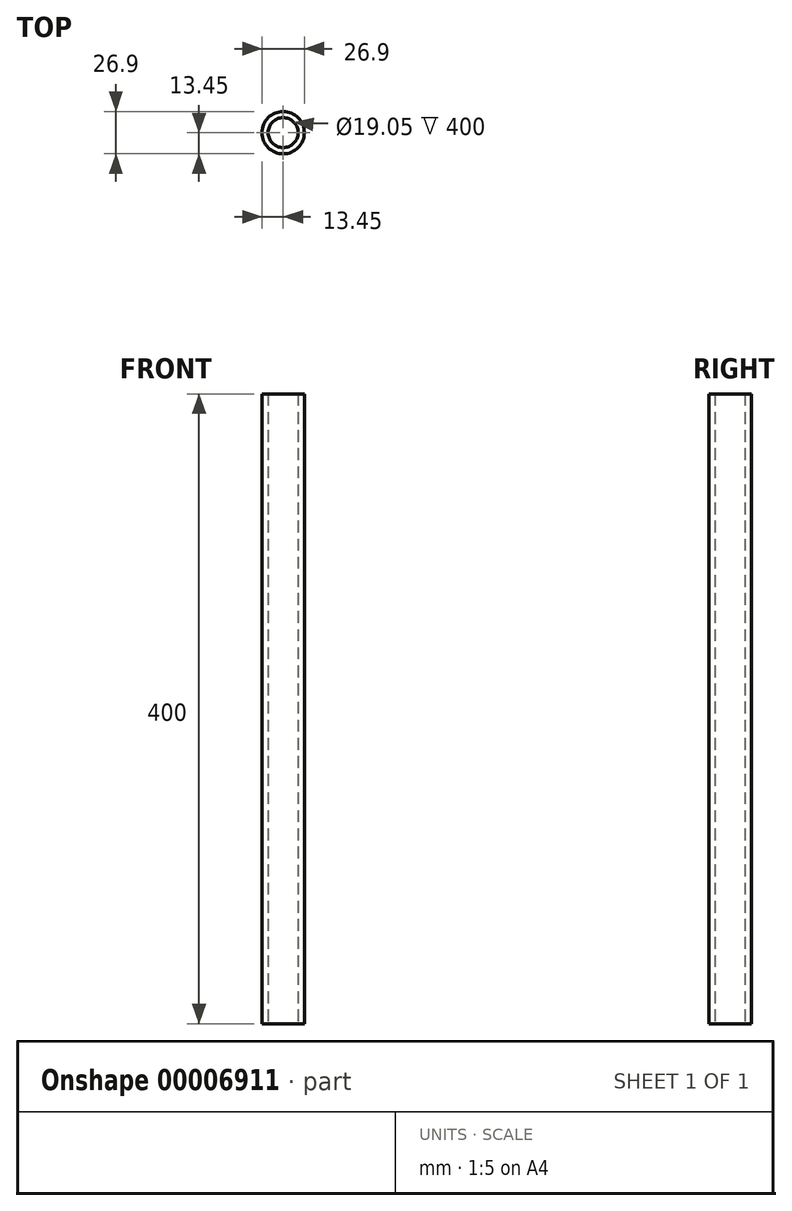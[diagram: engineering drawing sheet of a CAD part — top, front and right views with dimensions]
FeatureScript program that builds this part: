
annotation { "Feature Type Name" : "Feature", "Feature Type Description" : "" }
export const myFeature = defineFeature(function(context is Context, id is Id, definition is map)
    precondition{}
    {
        {
            var Q0;
            Q0=qCreatedBy(makeId("Top.planeOp"),FACE);
            var sketch = newSketch(context, id + "F0", { "sketchPlane" : qUnion([Q0])});
            skCircle(sketch, "E0", {"center": v(0, 0) * mm, "radius": 13.45 * mm});
            skCircle(sketch, "E1", {"center": v(0, 0) * mm, "radius": 9.53 * mm});
            skSolve(sketch);
        }
        {
            var Q0;
            Q0=makeQuery(id+"F0.imprint","IMPRINT",FACE,{"disambiguationData":[TD([[makeQuery(id+"F0.imprint","IMPRINT",EDGE,{"derivedFrom":sQuery(id+"F0.wireOp",EDGE,"E0")}),1.0]])]});
            extrude(context, id + "F1", {"entities" : qUnion([Q0]), "depth" : (400) * mm});
        }
    });
